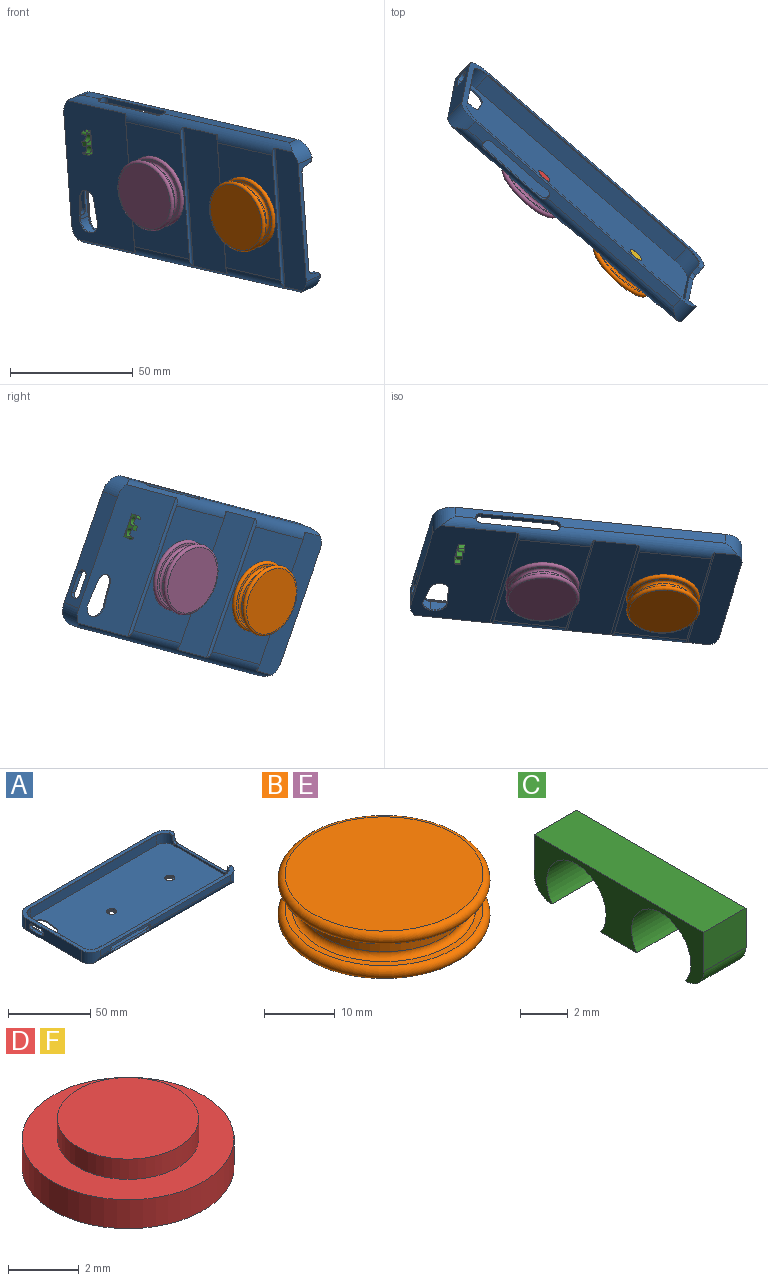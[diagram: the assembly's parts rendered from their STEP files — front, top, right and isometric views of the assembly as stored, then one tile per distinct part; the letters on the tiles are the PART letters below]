
ASSEMBLY  parts=6 mates=5
PART A: 84 faces, bbox 128.1x64x9.6 mm
  f0: cylinder r=2mm len=4mm, axis (0,0,-1), area 7.5mm2, adj f73,f82
  f1: cylinder r=2mm len=4mm, axis (0,0,-1), area 7.5mm2, adj f72,f80
  f2: plane 60x12.07mm, normal (0,0,-1), area 715.6mm2, adj f57,f58,f59,f75,f78,f79
  f3: plane 60x18mm, normal (0,0,-1), area 1080mm2, adj f74,f77,f78,f79
  f4: plane 124x59.8mm, normal (0,0,1), area 7165.6mm2, adj f10,f18,f19,f20,f22,f23,f24,f25
  f5: plane 60x34mm, normal (0,0,-1), area 1885.3mm2, adj f6,f35,f60,f61,f69,f70,f71,f76
  f6: plane 48x8.6mm, normal (-1,0,0), area 362.2mm2, adj f5,f7,f21,f26,f27,f28,f29,f60
  f7: plane 2.1x0.5mm, normal (0,1,0), area 1mm2, adj f6,f18,f26,f66
  f8: plane 112.2x4.6mm, normal (0,-1,0), area 426.8mm2, adj f21,f30,f31,f32,f33,f34,f59,f60
  f9: cylinder r=2mm len=3.19mm, axis (1,0,0), area 7mm2, adj f14,f15,f16,f17,f21,f24,f55,f57
  f10: cylinder r=7.5mm len=7.5mm, axis (0,0,1), area 81.5mm2, adj f4,f13,f20,f25,f51,f52,f56
  f11: cylinder r=7.09mm len=6.66mm, axis (0,0,-1), area 1.6mm2, adj f12,f21,f48,f56
  f12: torus R=7.29mm, axis (0,0,-1), area 2.8mm2, adj f11,f17,f49,f56
  f13: torus R=7.3mm, axis (0,0,-1), area 3mm2, adj f10,f17,f50,f56
  f14: cylinder r=7.09mm len=6.66mm, axis (0,0,-1), area 1.6mm2, adj f9,f15,f21,f36
  f15: torus R=7.29mm, axis (0,0,-1), area 2.8mm2, adj f9,f14,f17,f37
  f16: torus R=7.3mm, axis (0,0,-1), area 3mm2, adj f9,f17,f24,f38
  f17: plane 123.29x59.4mm, normal (0,0,-1), area 3mm2, adj f9,f12,f13,f15,f16,f37,f38,f40
  f18: plane 44.8x7.4mm, normal (1,0,0), area 281mm2, adj f4,f7,f22,f23,f26,f27,f28,f29
  f19: plane 109x7.4mm, normal (0,-1,0), area 806.6mm2, adj f4,f23,f24,f38
  f20: plane 44.8x1.8mm, normal (-1,0,0), area 63mm2, adj f4,f10,f24,f52,f53,f54
  f21: plane 128.02x64mm, normal (0,0,1), area 797.3mm2, adj f6,f8,f9,f11,f14,f36,f39,f42
  f22: cylinder r=7.5mm len=7.5mm, axis (0,0,1), area 87.2mm2, adj f4,f18,f25,f47
  f23: cylinder r=7.5mm len=7.5mm, axis (0,0,1), area 87.2mm2, adj f4,f18,f19,f41
  f24: cylinder r=7.5mm len=7.5mm, axis (0,0,1), area 81.5mm2, adj f4,f9,f16,f19,f20,f54,f55
  f25: plane 109x7.4mm, normal (0,1,0), area 652.5mm2, adj f4,f10,f22,f30,f31,f32,f33,f34
  f26: cylinder r=2mm len=2.1mm, axis (1,0,0), area 6.6mm2, adj f6,f7,f18,f27
  f27: plane 8x2.1mm, normal (0,0,-1), area 16.8mm2, adj f6,f18,f26,f28
  f28: cylinder r=2mm len=2.1mm, axis (1,0,0), area 6.6mm2, adj f6,f18,f27,f29
  f29: plane 2.1x0.5mm, normal (0,-1,0), area 1mm2, adj f6,f18,f28,f68
  f30: cylinder r=2mm len=2.1mm, axis (0,1,0), area 6.6mm2, adj f8,f25,f31,f34
  f31: plane 2.1x0.5mm, normal (1,0,0), area 1mm2, adj f8,f25,f30,f63
  f32: plane 2.1x0.5mm, normal (-1,0,0), area 1mm2, adj f8,f25,f33,f65
  f33: cylinder r=2mm len=2.1mm, axis (0,1,0), area 6.6mm2, adj f8,f25,f32,f34
  f34: plane 31x2.1mm, normal (0,0,-1), area 65.1mm2, adj f8,f25,f30,f33
  f35: cylinder r=5mm len=10mm, axis (0,0,-1), area 9.4mm2, adj f4,f5,f70,f71
  f36: plane 109x0.2mm, normal (0,-1,0), area 21.8mm2, adj f14,f21,f37,f39
  f37: cylinder r=0.2mm len=109mm, axis (1,0,0), area 34.2mm2, adj f15,f17,f36,f40
  f38: cylinder r=0.2mm len=109mm, axis (1,0,0), area 34.2mm2, adj f16,f17,f19,f41
  f39: cylinder r=7.09mm len=7.09mm, axis (0,0,-1), area 2.2mm2, adj f21,f36,f40,f42
  f40: torus R=7.29mm, axis (0,0,-1), area 3.5mm2, adj f17,f37,f39,f43
  f41: torus R=7.3mm, axis (0,0,-1), area 3.7mm2, adj f17,f23,f38,f44
  f42: plane 44.8x0.2mm, normal (1,0,0), area 9mm2, adj f21,f39,f43,f45
  f43: cylinder r=0.2mm len=44.8mm, axis (0,1,0), area 14.1mm2, adj f17,f40,f42,f46
  f44: cylinder r=0.2mm len=44.8mm, axis (0,1,0), area 14.1mm2, adj f17,f18,f41,f47
  f45: cylinder r=7.09mm len=7.09mm, axis (0,0,-1), area 2.2mm2, adj f21,f42,f46,f48
  f46: torus R=7.29mm, axis (0,0,-1), area 3.5mm2, adj f17,f43,f45,f49
  f47: torus R=7.3mm, axis (0,0,-1), area 3.7mm2, adj f17,f22,f44,f50
  f48: plane 109x0.2mm, normal (0,1,0), area 21.8mm2, adj f11,f21,f45,f49
  f49: cylinder r=0.2mm len=109mm, axis (1,0,0), area 34.2mm2, adj f12,f17,f46,f48
  f50: cylinder r=0.2mm len=109mm, axis (1,0,0), area 34.2mm2, adj f13,f17,f25,f47
  f51: plane 3.27x2.1mm, normal (0,0.99,0.17), area 6.8mm2, adj f10,f52,f56,f58
  f52: cylinder r=2mm len=2.01mm, axis (1,0,0), area 5.6mm2, adj f10,f20,f51,f53,f58
  f53: plane 42.4x1.97mm, normal (0,0,1), area 83.6mm2, adj f20,f52,f54,f58
  f54: cylinder r=2mm len=2.01mm, axis (1,0,0), area 5.6mm2, adj f20,f24,f53,f55,f58
  f55: plane 3.27x2.1mm, normal (0,-0.99,0.17), area 6.8mm2, adj f9,f24,f54,f58
  f56: cylinder r=2mm len=3.19mm, axis (1,0,0), area 7mm2, adj f10,f11,f12,f13,f17,f21,f51,f58
  f57: cylinder r=8mm len=8.6mm, axis (0,0,1), area 85mm2, adj f2,f9,f21,f58,f62,f79
  f58: plane 50.85x8.58mm, normal (1,0,0), area 127.8mm2, adj f2,f9,f51,f52,f53,f54,f55,f56
  f59: cylinder r=8mm len=8.6mm, axis (0,0,1), area 85mm2, adj f2,f8,f21,f56,f58,f78
  f60: cylinder r=8mm len=8.6mm, axis (0,0,1), area 97.3mm2, adj f5,f6,f8,f21,f78
  f61: cylinder r=8mm len=8.6mm, axis (0,0,1), area 97.3mm2, adj f5,f6,f21,f62,f79
  f62: plane 112.2x4.6mm, normal (0,1,0), area 516.1mm2, adj f21,f57,f61,f79
  f63: cylinder r=2mm len=2.1mm, axis (0,1,0), area 6mm2, adj f8,f25,f31,f64,f78
  f64: plane 31x1.73mm, normal (0,0,1), area 53.5mm2, adj f25,f63,f65,f78
  f65: cylinder r=2mm len=2.1mm, axis (0,1,0), area 6mm2, adj f8,f25,f32,f64,f78
  f66: cylinder r=2mm len=2.1mm, axis (1,0,0), area 6.6mm2, adj f6,f7,f18,f67
  f67: plane 8x2.1mm, normal (0,0,1), area 16.8mm2, adj f6,f18,f66,f68
  f68: cylinder r=2mm len=2.1mm, axis (1,0,0), area 6.6mm2, adj f6,f18,f29,f67
  f69: cylinder r=3.75mm len=7.46mm, axis (0,0,1), area 6.6mm2, adj f4,f5,f70,f71
  f70: plane 9.98x1.28mm, normal (-0.99,0.13,0), area 6mm2, adj f4,f5,f35,f69
  f71: plane 9.83x1.26mm, normal (0.99,0.13,0), area 5.9mm2, adj f4,f5,f35,f69
  f72: plane 54x30mm, normal (0,0,-1), area 1607.4mm2, adj f1,f76,f77,f78,f79
  f73: plane 54x30mm, normal (0,0,-1), area 1607.4mm2, adj f0,f74,f75,f78,f79
  f74: cylinder r=1mm len=60mm, axis (0,1,0), area 92.1mm2, adj f3,f73,f78,f79
  f75: cylinder r=1mm len=60mm, axis (0,-1,0), area 92.1mm2, adj f2,f73,f78,f79
  f76: cylinder r=1mm len=60mm, axis (0,1,0), area 92.1mm2, adj f5,f72,f78,f79
  f77: cylinder r=1mm len=60mm, axis (0,-1,0), area 92.1mm2, adj f3,f72,f78,f79
  f78: cylinder r=5mm len=122.78mm, axis (-1,0,0), area 674.3mm2, adj f2,f3,f5,f8,f59,f60,f63,f64
  f79: cylinder r=5mm len=122.78mm, axis (1,0,0), area 740.8mm2, adj f2,f3,f5,f57,f61,f62,f72,f73
  f80: plane 6x6mm, normal (0,0,1), area 15.7mm2, adj f1,f81
  f81: cylinder r=3mm len=6mm, axis (0,0,1), area 18.8mm2, adj f4,f80
  f82: plane 6x6mm, normal (0,0,1), area 15.7mm2, adj f0,f83
  f83: cylinder r=3mm len=6mm, axis (0,0,1), area 18.8mm2, adj f4,f82
PART B: 9 faces, bbox 32.5x32.5x8 mm
  f0: plane 28x28mm, normal (0,0,1), area 84.8mm2, adj f5,f8
  f1: cylinder r=12mm len=24mm, axis (0,0,-1), area 150.8mm2, adj f5,f6
  f2: plane 28x28mm, normal (0,0,-1), area 84.8mm2, adj f6,f7
  f3: plane 28x28mm, normal (0,0,1), area 615.8mm2, adj f7
  f4: plane 28x28mm, normal (0,0,-1), area 615.8mm2, adj f8
  f5: torus R=13mm, axis (0,0,-1), area 122mm2, adj f0,f1
  f6: torus R=13mm, axis (0,0,-1), area 122mm2, adj f1,f2
  f7: torus R=14mm, axis (0,0,-1), area 288.9mm2, adj f2,f3
  f8: torus R=14mm, axis (0,0,-1), area 288.9mm2, adj f0,f4
PART C: 12 faces, bbox 2.5x10x3 mm
  f0: cylinder r=1.75mm len=3.5mm, axis (-1,0,0), area 19.1mm2, adj f1,f9,f10,f11
  f1: plane 2.5x2.13mm, normal (0,0,-1), area 5.3mm2, adj f0,f2,f10,f11
  f2: cylinder r=1.75mm len=3.5mm, axis (-1,0,0), area 19.1mm2, adj f1,f3,f10,f11
  f3: plane 2.5x0.06mm, normal (0,0,-1), area 0.2mm2, adj f2,f4,f10,f11
  f4: cylinder r=1mm len=2.5mm, axis (-1,0,0), area 3.9mm2, adj f3,f5,f10,f11
  f5: plane 2.5x2mm, normal (0,1,0), area 5mm2, adj f4,f6,f10,f11
  f6: plane 10x2.5mm, normal (0,0,1), area 25mm2, adj f5,f7,f10,f11
  f7: plane 2.5x2mm, normal (0,-1,0), area 5mm2, adj f6,f8,f10,f11
  f8: cylinder r=1mm len=2.5mm, axis (-1,0,0), area 3.9mm2, adj f7,f9,f10,f11
  f9: plane 2.5x0.06mm, normal (0,0,-1), area 0.2mm2, adj f0,f8,f10,f11
  f10: plane 10x3mm, normal (1,0,0), area 13.4mm2, adj f0,f1,f2,f3,f4,f5,f6,f7
  f11: plane 10x3mm, normal (-1,0,0), area 13.4mm2, adj f0,f1,f2,f3,f4,f5,f6,f7
PART D: 5 faces, bbox 6x6x1.7 mm
  f0: plane 6x6mm, normal (0,0,-1), area 28.3mm2, adj f1
  f1: cylinder r=3mm len=6mm, axis (0,0,1), area 18.8mm2, adj f0,f2
  f2: plane 6x6mm, normal (0,0,1), area 15.7mm2, adj f1,f3
  f3: cylinder r=2mm len=4mm, axis (0,0,1), area 8.8mm2, adj f2,f4
  f4: plane 4x4mm, normal (0,0,1), area 12.6mm2, adj f3
PART E: same geometry as B
PART F: same geometry as D
PLACE A rot(axis=(-0.83,0.42,-0.36),79.6deg) t=(-55,58.13,77.5)mm
PLACE B rot(axis=(0.34,0.5,0.8),165.2deg) t=(15.28,-1.87,28.13)mm
PLACE C rot(axis=(-0.83,0.42,-0.36),79.6deg) t=(-52.18,58.66,73.18)mm
PLACE D rot(axis=(-0.24,-0.8,0.55),148.5deg) t=(-6.21,58.25,47.53)mm
PLACE E rot(axis=(-0.83,0.42,-0.36),79.6deg) t=(-22.02,30.3,36.71)mm
PLACE F rot(axis=(0.91,-0.15,-0.39),121.1deg) t=(43.03,16.58,34.28)mm
MATE fastened A.f5 <-> C.f6  axis (-0.66,-0.69,-0.29) through (-44.52,55.82,58.86)mm
MATE fastened E.f1 <-> D.f1  axis (0.66,0.69,0.29) through (-16.72,35.84,39)mm
MATE revolute A.f1 <-> D.f1  axis (0.66,0.69,0.29) through (-16.26,36.32,39.2)mm
MATE revolute A.f0 <-> F.f1  axis (0.66,0.69,0.29) through (21.04,4.15,30.63)mm
MATE fastened B.f1 <-> F.f1  axis (0.66,0.69,0.29) through (20.58,3.66,30.43)mm
